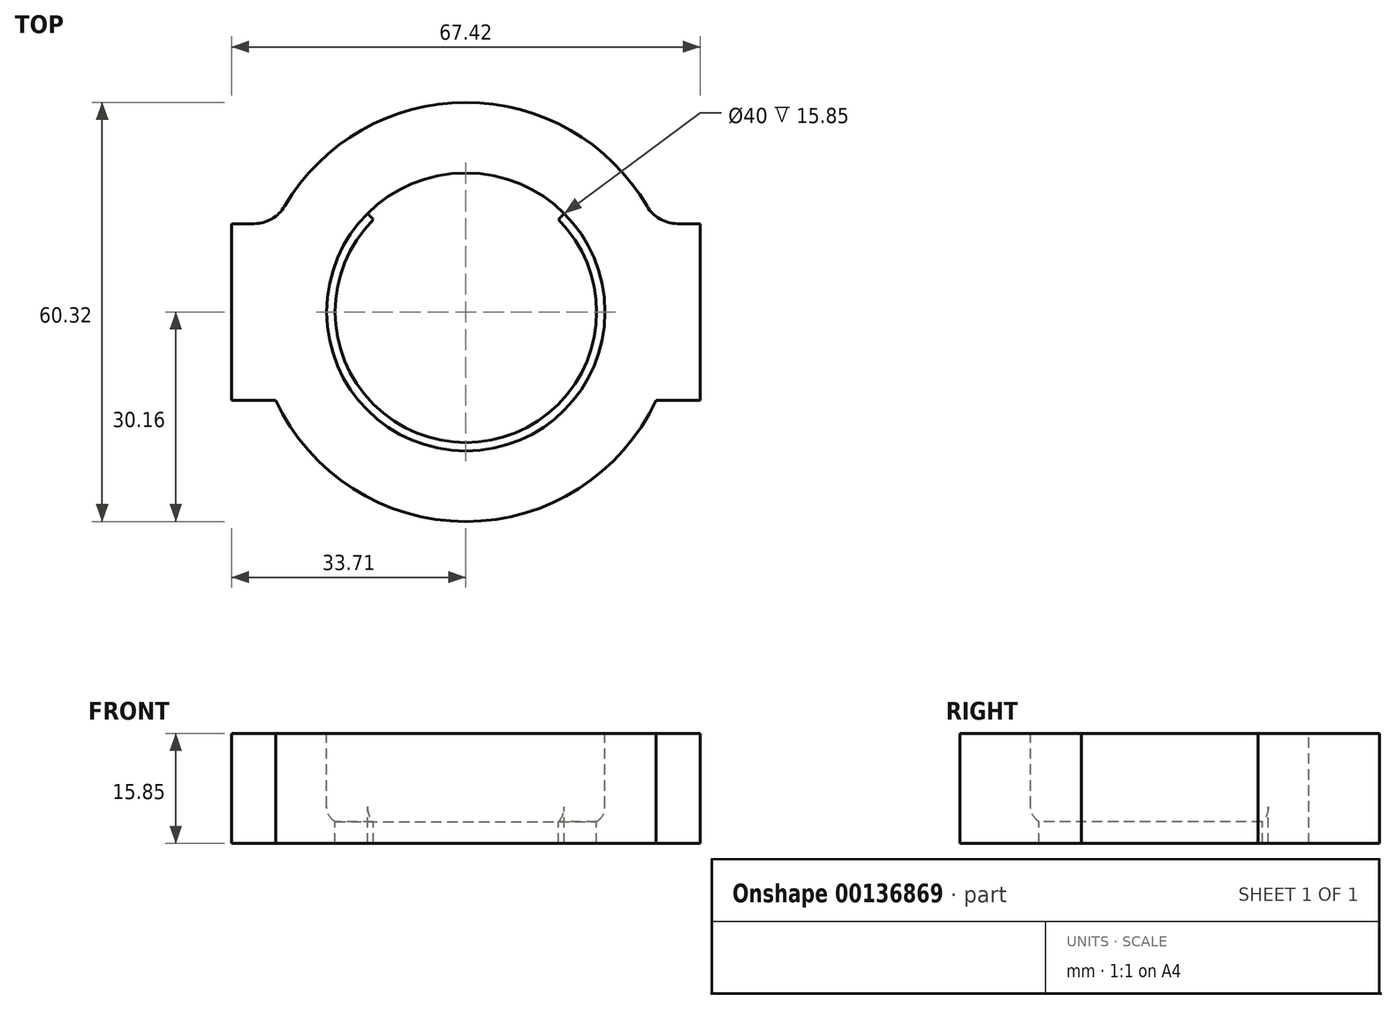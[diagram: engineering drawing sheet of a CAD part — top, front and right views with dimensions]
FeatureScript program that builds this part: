
annotation { "Feature Type Name" : "Feature", "Feature Type Description" : "" }
export const myFeature = defineFeature(function(context is Context, id is Id, definition is map)
    precondition{}
    {
        {
            var Q0;
            Q0=qCreatedBy(makeId("Front.planeOp"),FACE);
            var sketch = newSketch(context, id + "F0", { "sketchPlane" : qUnion([Q0])});
            skLineSegment(sketch, "E0", {"start": v(18.8, 0) * mm, "end": v(18.8, 3.15) * mm});
            skLineSegment(sketch, "E1", {"start": v(18.8, 3.15) * mm, "end": v(20, 3.15) * mm});
            skLineSegment(sketch, "E2", {"start": v(20, 3.15) * mm, "end": v(20, 15.85) * mm});
            skLineSegment(sketch, "E3", {"start": v(20, 15.85) * mm, "end": v(30.16, 15.85) * mm});
            skLineSegment(sketch, "E4", {"start": v(30.16, 15.85) * mm, "end": v(30.16, 0) * mm});
            skLineSegment(sketch, "E5", {"start": v(30.16, 0) * mm, "end": v(18.8, 0) * mm});
            skLineSegment(sketch, "E6", {"start": v(0, 29.7) * mm, "end": v(0, 0) * mm, "construction": true});
            skSolve(sketch);
        }
        {
            var Q0;
            Q0=makeQuery(id+"F0.imprint","IMPRINT",FACE,{"disambiguationData":[TD([[makeQuery(id+"F0.imprint","IMPRINT",EDGE,{"derivedFrom":sQuery(id+"F0.wireOp",EDGE,"E0")}),-1.0]])]});
            var Q1;
            Q1=sQuery(id+"F0.wireOp",EDGE,"E6");
            revolve(context, id + "F1", {"entities" : qUnion([Q0]), "axis" : qUnion([Q1]), "revolveType" : RevolveType.FULL});
        }
        {
            var Q0;
            Q0=makeQuery(id+"F1.opRevolve","SWEPT_FACE",FACE,{"disambiguationData":[OSD([sQuery(id+"F0.wireOp",EDGE,"E1")])]});
            var sketch = newSketch(context, id + "F2", { "sketchPlane" : qUnion([Q0])});
            skLineSegment(sketch, "E7", {"start": v(-14.14, 14.14) * mm, "end": v(0, 0) * mm});
            skLineSegment(sketch, "E8", {"start": v(0, 0) * mm, "end": v(14.14, 14.14) * mm});
            skCircle(sketch, "E9", {"center": v(0, 0) * mm, "radius": 20 * mm});
            skSolve(sketch);
        }
        {
            var Q0;
            {var subQ0=sQuery(id+"F2.wireOp",EDGE,"E9");var subQ1=sQuery(id+"F2.wireOp",EDGE,"E7");var subQ2=makeQuery(id+"F2.imprint","INTERSECT",VERTEX,{"derivedFrom":[subQ1,subQ0]});Q0=makeQuery(id+"F2.imprint","IMPRINT",FACE,{"disambiguationData":[TD([[makeQuery(id+"F2.imprint","IMPRINT",EDGE,{"disambiguationData":[TD([[subQ2,1.0]])],"derivedFrom":subQ0}),1.0]])]});}
            extrude(context, id + "F3", {"entities" : qUnion([Q0]), "operationType" : NewBodyOperationType.REMOVE, "oppositeDirection" : true, "depth" : 25.4 * mm});
        }
        {
            var Q0;
            Q0=qCreatedBy(makeId("Top.planeOp"),FACE);
            var sketch = newSketch(context, id + "F4", { "sketchPlane" : qUnion([Q0])});
            skLineSegment(sketch, "E10.bottom", {"start": v(-27.36, 12.7) * mm, "end": v(-33.7, 12.7) * mm});
            skLineSegment(sketch, "E10.top", {"start": v(-27.36, -12.7) * mm, "end": v(-33.7, -12.7) * mm});
            skLineSegment(sketch, "E10.left", {"start": v(-27.36, 12.7) * mm, "end": v(-27.36, -12.7) * mm});
            skLineSegment(sketch, "E10.right", {"start": v(-33.7, 12.7) * mm, "end": v(-33.7, -12.7) * mm});
            skLineSegment(sketch, "E11.MirrorCS", {"start": v(33.7, 12.7) * mm, "end": v(33.7, -12.7) * mm});
            skLineSegment(sketch, "E12.MirrorCS", {"start": v(27.36, 12.7) * mm, "end": v(33.7, 12.7) * mm});
            skLineSegment(sketch, "E13.MirrorCS", {"start": v(27.36, -12.7) * mm, "end": v(33.7, -12.7) * mm});
            skLineSegment(sketch, "E14.MirrorCS", {"start": v(27.36, 12.7) * mm, "end": v(27.36, -12.7) * mm});
            skSolve(sketch);
        }
        {
            var Q0;
            Q0=makeQuery(id+"F4.imprint","IMPRINT",FACE,{"disambiguationData":[TD([[makeQuery(id+"F4.imprint","IMPRINT",EDGE,{"derivedFrom":sQuery(id+"F4.wireOp",EDGE,"E10.bottom")}),1.0]])]});
            var Q1;
            Q1=makeQuery(id+"F4.imprint","IMPRINT",FACE,{"disambiguationData":[TD([[makeQuery(id+"F4.imprint","IMPRINT",EDGE,{"derivedFrom":sQuery(id+"F4.wireOp",EDGE,"E11.MirrorCS")}),-1.0]])]});
            var Q2;
            Q2=makeQuery(id+"F1.opRevolve","SWEPT_FACE",FACE,{"disambiguationData":[OSD([sQuery(id+"F0.wireOp",EDGE,"E3")])]});
            extrude(context, id + "F5", {"entities" : qUnion([Q0, Q1]), "operationType" : NewBodyOperationType.ADD, "endBound" : BoundingType.UP_TO_SURFACE, "endBoundEntityFace" : qUnion([Q2]), "depth" : 25.4 * mm});
        }
        {
            var Q0;
            Q0=makeQuery(id+"F5.opExtrude","SWEPT_EDGE",EDGE,{"disambiguationData":[OSD([sQuery(id+"F4.wireOp",EDGE,"E10.top"),sQuery(id+"F4.wireOp",EDGE,"E10.left")])]});
            var Q1;
            Q1=makeQuery(id+"F5.opExtrude","SWEPT_EDGE",EDGE,{"disambiguationData":[OSD([sQuery(id+"F4.wireOp",EDGE,"E13.MirrorCS"),sQuery(id+"F4.wireOp",EDGE,"E14.MirrorCS")])]});
            var Q2;
            Q2=makeQuery(id+"F5.opExtrude","SWEPT_EDGE",EDGE,{"disambiguationData":[OSD([sQuery(id+"F4.wireOp",EDGE,"E12.MirrorCS"),sQuery(id+"F4.wireOp",EDGE,"E14.MirrorCS")])]});
            var Q3;
            Q3=makeQuery(id+"F5.opExtrude","SWEPT_EDGE",EDGE,{"disambiguationData":[OSD([sQuery(id+"F4.wireOp",EDGE,"E10.bottom"),sQuery(id+"F4.wireOp",EDGE,"E10.left")])]});
            fillet(context, id + "F6", {"entities" : qUnion([Q0, Q1, Q2, Q3]), "radius" : 5.08 * mm, "tangentPropagation" : true, "allowEdgeOverflow" : false});
        }
        {
            var Q0;
            Q0=makeQuery(id+"F1.opRevolve","SWEPT_EDGE",EDGE,{"disambiguationData":[OSD([sQuery(id+"F0.wireOp",EDGE,"E1"),sQuery(id+"F0.wireOp",EDGE,"E2")])]});
            fillet(context, id + "F7", {"entities" : qUnion([Q0]), "radius" : 2.54 * mm, "tangentPropagation" : true, "allowEdgeOverflow" : false});
        }
    });
